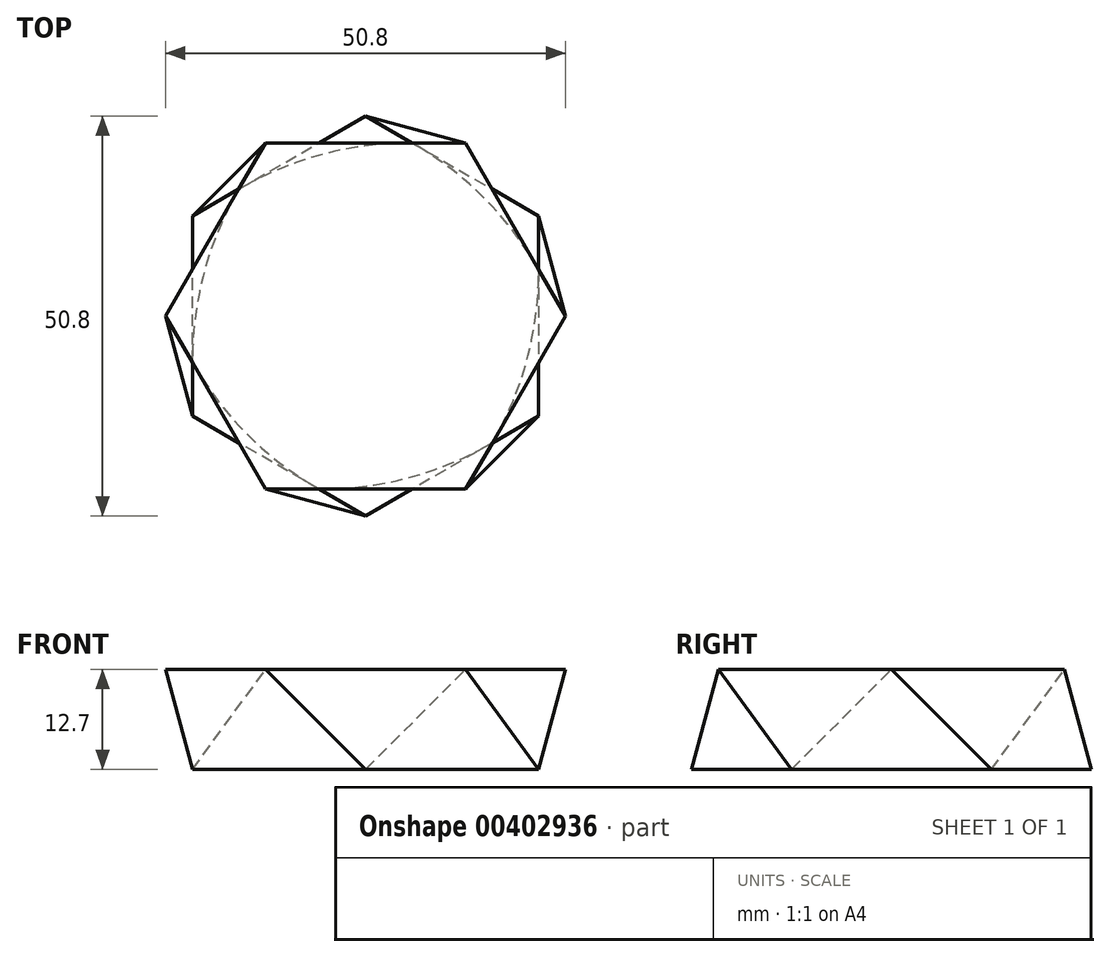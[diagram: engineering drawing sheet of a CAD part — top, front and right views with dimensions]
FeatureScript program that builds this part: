
annotation { "Feature Type Name" : "Feature", "Feature Type Description" : "" }
export const myFeature = defineFeature(function(context is Context, id is Id, definition is map)
    precondition{}
    {
        {
            var Q0;
            Q0=qCreatedBy(makeId("Top.planeOp"),FACE);
            var sketch = newSketch(context, id + "F0", { "sketchPlane" : qUnion([Q0])});
            skCircle(sketch, "E0.cCircle", {"center": v(0, 0) * mm, "radius": 22 * mm, "construction": true});
            skLineSegment(sketch, "E0.0", {"start": v(22, 12.7) * mm, "end": v(22, -12.7) * mm});
            skLineSegment(sketch, "E0.1", {"start": v(22, -12.7) * mm, "end": v(0, -25.4) * mm});
            skLineSegment(sketch, "E0.2", {"start": v(0, -25.4) * mm, "end": v(-22, -12.7) * mm});
            skLineSegment(sketch, "E0.3", {"start": v(-22, -12.7) * mm, "end": v(-22, 12.7) * mm});
            skLineSegment(sketch, "E0.4", {"start": v(-22, 12.7) * mm, "end": v(0, 25.4) * mm});
            skLineSegment(sketch, "E0.5", {"start": v(0, 25.4) * mm, "end": v(22, 12.7) * mm});
            skPoint(sketch, "E0.0.midPoint", {"position": v(22, 0) * mm});
            skSolve(sketch);
        }
        {
            var Q0;
            Q0=qCreatedBy(makeId("Top.planeOp"),FACE);
            cPlane(context, id + "F1", {"entities" : qUnion([Q0]), "cplaneType" : CPlaneType.OFFSET, "offset" : 12.7 * mm, "width" : 152.4 * mm, "height" : 152.4 * mm});
        }
        {
            var Q0;
            Q0=qCreatedBy(id+"F1.planeOp",FACE);
            var sketch = newSketch(context, id + "F2", { "sketchPlane" : qUnion([Q0])});
            skCircle(sketch, "E1.cCircle", {"center": v(0, 0) * mm, "radius": 22 * mm, "construction": true});
            skLineSegment(sketch, "E1.0", {"start": v(-25.4, 0) * mm, "end": v(-12.7, 22) * mm});
            skLineSegment(sketch, "E1.1", {"start": v(-12.7, 22) * mm, "end": v(12.7, 22) * mm});
            skLineSegment(sketch, "E1.2", {"start": v(12.7, 22) * mm, "end": v(25.4, 0) * mm});
            skLineSegment(sketch, "E1.3", {"start": v(25.4, 0) * mm, "end": v(12.7, -22) * mm});
            skLineSegment(sketch, "E1.4", {"start": v(12.7, -22) * mm, "end": v(-12.7, -22) * mm});
            skLineSegment(sketch, "E1.5", {"start": v(-12.7, -22) * mm, "end": v(-25.4, 0) * mm});
            skPoint(sketch, "E1.0.midPoint", {"position": v(-19.05, 11) * mm});
            skSolve(sketch);
        }
        {
            var Q0;
            Q0=makeQuery(id+"F0.imprint","IMPRINT",FACE,{"disambiguationData":[TD([[makeQuery(id+"F0.imprint","IMPRINT",EDGE,{"derivedFrom":sQuery(id+"F0.wireOp",EDGE,"E0.0")}),-1.0]])]});
            var Q1;
            Q1=makeQuery(id+"F2.imprint","IMPRINT",FACE,{"disambiguationData":[TD([[makeQuery(id+"F2.imprint","IMPRINT",EDGE,{"derivedFrom":sQuery(id+"F2.wireOp",EDGE,"E1.0")}),-1.0]])]});
            var Q2;
            Q2=sQuery(id+"F2.wireOp",VERTEX,"E1.5.start");
            var Q3;
            Q3=sQuery(id+"F0.wireOp",VERTEX,"E0.2.start");
            loft(context, id + "F3", {"sheetProfilesArray" : [{ "sheetProfileEntities" : qUnion([Q0]) }, { "sheetProfileEntities" : qUnion([Q1]) }], "matchConnections" : true, "connections" : [{ "connectionEntities" : qUnion([Q2, Q3]), "connectionEdgeQueries" : qUnion([]), "connectionEdgeParameters" : [] }]});
        }
    });
